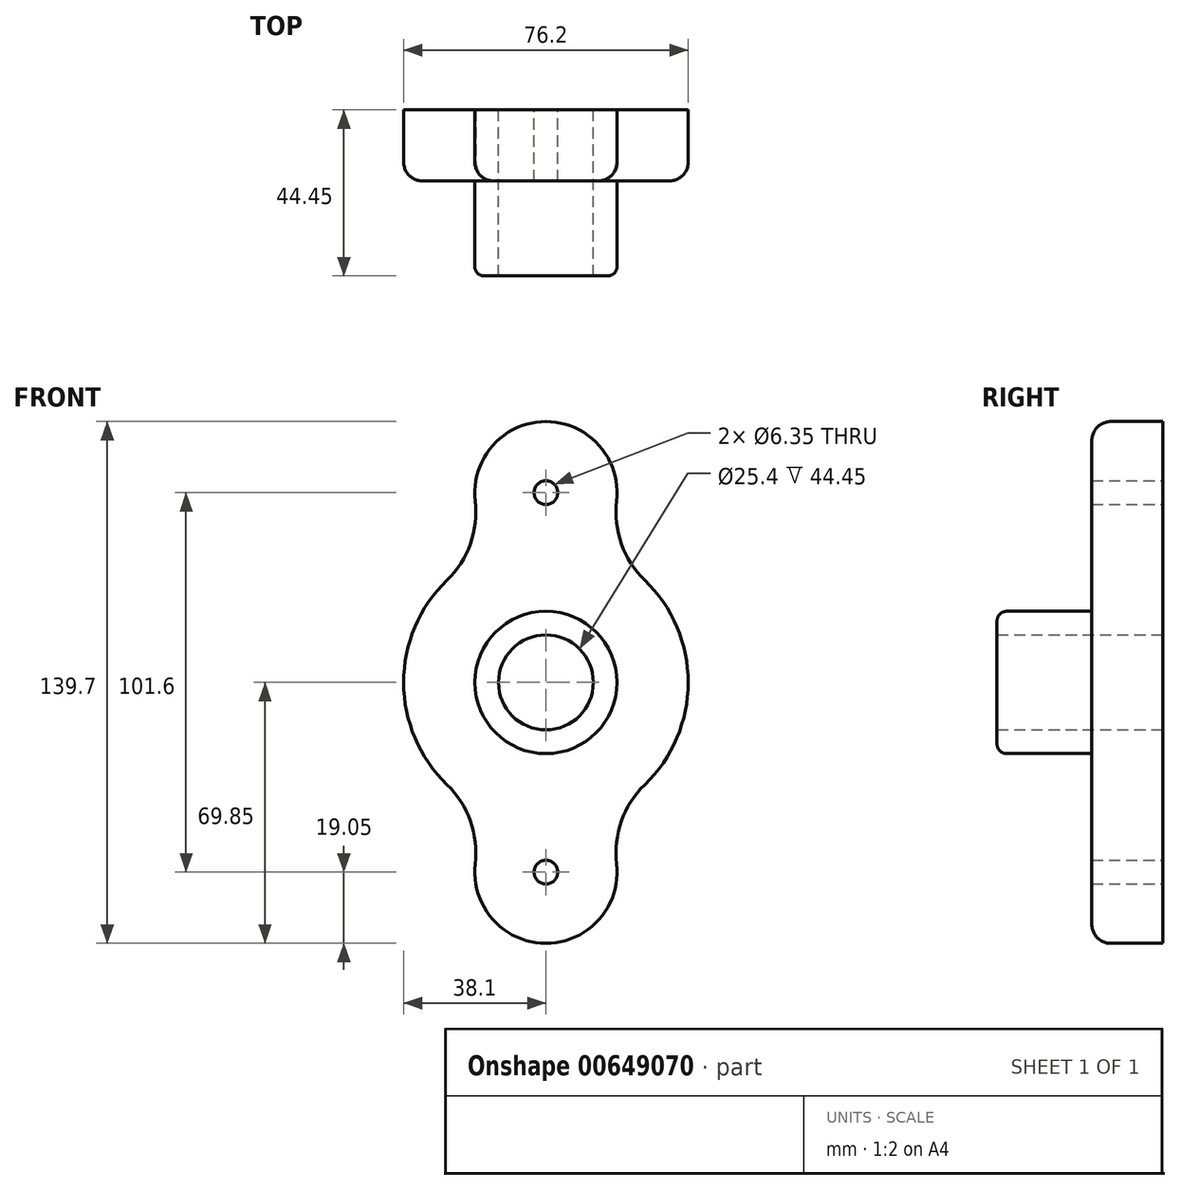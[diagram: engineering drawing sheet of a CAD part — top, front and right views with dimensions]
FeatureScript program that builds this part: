
annotation { "Feature Type Name" : "Feature", "Feature Type Description" : "" }
export const myFeature = defineFeature(function(context is Context, id is Id, definition is map)
    precondition{}
    {
        {
            var Q0;
            Q0=qCreatedBy(makeId("Front.planeOp"),FACE);
            var sketch = newSketch(context, id + "F0", { "sketchPlane" : qUnion([Q0])});
            skCircle(sketch, "E0", {"center": v(0, 0) * mm, "radius": 12.7 * mm});
            skLineSegment(sketch, "E1", {"start": v(0, -50.8) * mm, "end": v(0, 50.8) * mm, "construction": true});
            skArc(sketch, "E2", {"start": v(12.14, 36.12) * mm, "mid": v(0, 69.85) * mm, "end": v(-12.14, 36.12) * mm});
            skArc(sketch, "E3", {"start": v(-12.14, -36.12) * mm, "mid": v(0, -69.85) * mm, "end": v(12.14, -36.12) * mm});
            skArc(sketch, "E4", {"start": v(-12.14, 36.12) * mm, "mid": v(-38.1, 0) * mm, "end": v(-12.14, -36.12) * mm});
            skArc(sketch, "E5.trimOffspring", {"start": v(12.14, -36.12) * mm, "mid": v(38.1, 0) * mm, "end": v(12.14, 36.12) * mm});
            skCircle(sketch, "E6", {"center": v(0, 50.8) * mm, "radius": 3.18 * mm});
            skCircle(sketch, "E7", {"center": v(0, -50.8) * mm, "radius": 3.18 * mm});
            skSolve(sketch);
        }
        {
            var Q0;
            Q0 = qSketchRegion(id + "F0", true);
            extrude(context, id + "F1", {"entities" : qUnion([Q0]), "depth" : 19.05 * mm, "offsetDistance" : 25.4 * mm});
        }
        {
            var Q0;
            Q0=makeQuery(id+"F1.opExtrude","SWEPT_EDGE",EDGE,{"disambiguationData":[OSD([sQuery(id+"F0.wireOp",EDGE,"E2"),sQuery(id+"F0.wireOp",EDGE,"E5.trimOffspring")])]});
            var Q1;
            Q1=makeQuery(id+"F1.opExtrude","SWEPT_EDGE",EDGE,{"disambiguationData":[OSD([sQuery(id+"F0.wireOp",EDGE,"E3"),sQuery(id+"F0.wireOp",EDGE,"E5.trimOffspring")])]});
            var Q2;
            Q2=makeQuery(id+"F1.opExtrude","SWEPT_EDGE",EDGE,{"disambiguationData":[OSD([sQuery(id+"F0.wireOp",EDGE,"E3"),sQuery(id+"F0.wireOp",EDGE,"E4")])]});
            var Q3;
            Q3=makeQuery(id+"F1.opExtrude","SWEPT_EDGE",EDGE,{"disambiguationData":[OSD([sQuery(id+"F0.wireOp",EDGE,"E2"),sQuery(id+"F0.wireOp",EDGE,"E4")])]});
            fillet(context, id + "F2", {"entities" : qUnion([Q0, Q1, Q2, Q3]), "radius" : 25.4 * mm, "tangentPropagation" : true, "allowEdgeOverflow" : false});
        }
        {
            var Q0;
            {var subQ0=sQuery(id+"F0.wireOp",EDGE,"E4");var subQ1=sQuery(id+"F0.wireOp",EDGE,"E2");Q0=makeQuery(id+"F2.opFillet","BLEND_EDGE",EDGE,{"blendedFrom":[makeQuery(id+"F1.opExtrude","SWEPT_EDGE",EDGE,{"disambiguationData":[OSD([subQ1,subQ0])]}),makeQuery(id+"F1.opExtrude","CAP_FACE",FACE,{"disambiguationData":[OSD([sQuery(id+"F0.wireOp",EDGE,"E0"),subQ1,sQuery(id+"F0.wireOp",EDGE,"E3"),subQ0,sQuery(id+"F0.wireOp",EDGE,"E5.trimOffspring"),sQuery(id+"F0.wireOp",EDGE,"E6"),sQuery(id+"F0.wireOp",EDGE,"E7")])],"isStart":false})],"blendedInto":[makeQuery(id+"F1.opExtrude","CAP_FACE",FACE,{"disambiguationData":[OSD([sQuery(id+"F0.wireOp",EDGE,"E0"),subQ1,sQuery(id+"F0.wireOp",EDGE,"E3"),subQ0,sQuery(id+"F0.wireOp",EDGE,"E5.trimOffspring"),sQuery(id+"F0.wireOp",EDGE,"E6"),sQuery(id+"F0.wireOp",EDGE,"E7")])],"isStart":false})]});}
            fillet(context, id + "F3", {"entities" : qUnion([Q0]), "radius" : 5.08 * mm, "tangentPropagation" : true, "allowEdgeOverflow" : false});
        }
        {
            var Q0;
            Q0=makeQuery(id+"F1.opExtrude","CAP_FACE",FACE,{"disambiguationData":[OSD([sQuery(id+"F0.wireOp",EDGE,"E0"),sQuery(id+"F0.wireOp",EDGE,"E2"),sQuery(id+"F0.wireOp",EDGE,"E3"),sQuery(id+"F0.wireOp",EDGE,"E4"),sQuery(id+"F0.wireOp",EDGE,"E5.trimOffspring"),sQuery(id+"F0.wireOp",EDGE,"E6"),sQuery(id+"F0.wireOp",EDGE,"E7")])],"isStart":false});
            var sketch = newSketch(context, id + "F4", { "sketchPlane" : qUnion([Q0])});
            skCircle(sketch, "E8", {"center": v(0, 0) * mm, "radius": 19.05 * mm});
            skCircle(sketch, "E9", {"center": v(0, 0) * mm, "radius": 12.7 * mm});
            skSolve(sketch);
        }
        {
            var Q0;
            Q0 = qSketchRegion(id + "F4", true);
            extrude(context, id + "F5", {"entities" : qUnion([Q0]), "operationType" : NewBodyOperationType.ADD, "depth" : 25.4 * mm, "offsetDistance" : 25.4 * mm});
        }
        {
            var Q0;
            Q0=makeQuery(id+"F5.opExtrude","CAP_EDGE",EDGE,{"disambiguationData":[OSD([sQuery(id+"F4.wireOp",EDGE,"E8")])],"isStart":false});
            fillet(context, id + "F6", {"entities" : qUnion([Q0]), "radius" : 2.54 * mm, "tangentPropagation" : true, "allowEdgeOverflow" : false});
        }
    });
